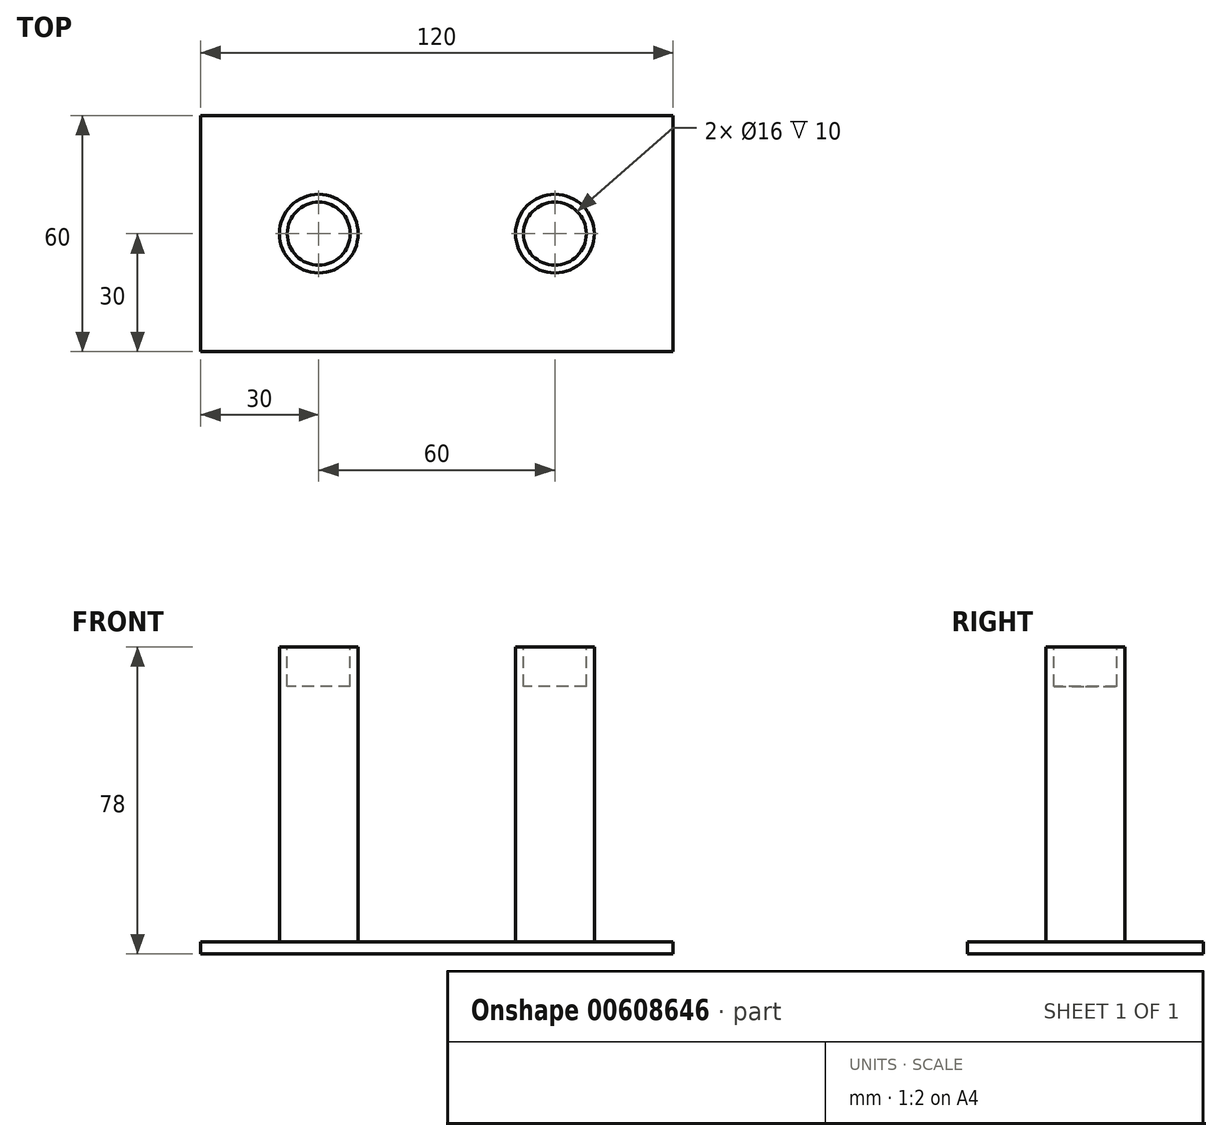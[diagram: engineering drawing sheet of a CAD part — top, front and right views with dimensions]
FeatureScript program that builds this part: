
annotation { "Feature Type Name" : "Feature", "Feature Type Description" : "" }
export const myFeature = defineFeature(function(context is Context, id is Id, definition is map)
    precondition{}
    {
        {
            var Q0;
            Q0=qCreatedBy(makeId("Top.planeOp"),FACE);
            var sketch = newSketch(context, id + "F0", { "sketchPlane" : qUnion([Q0])});
            skCircle(sketch, "E0", {"center": v(0, 0) * mm, "radius": 10 * mm});
            skLineSegment(sketch, "E1", {"start": v(0, 0) * mm, "end": v(-60, 0) * mm, "construction": true});
            skCircle(sketch, "E2", {"center": v(-60, 0) * mm, "radius": 10 * mm});
            skLineSegment(sketch, "E3.bottom", {"start": v(-90, 30) * mm, "end": v(30, 30) * mm});
            skLineSegment(sketch, "E3.top", {"start": v(-90, -30) * mm, "end": v(30, -30) * mm});
            skLineSegment(sketch, "E3.left", {"start": v(-90, 30) * mm, "end": v(-90, -30) * mm});
            skLineSegment(sketch, "E3.right", {"start": v(30, 30) * mm, "end": v(30, -30) * mm});
            skSolve(sketch);
        }
        {
            var Q0;
            Q0=makeQuery(id+"F0.imprint","IMPRINT",FACE,{"disambiguationData":[TD([[makeQuery(id+"F0.imprint","IMPRINT",EDGE,{"derivedFrom":sQuery(id+"F0.wireOp",EDGE,"E0")}),-1.0]])]});
            var Q1;
            Q1=makeQuery(id+"F0.imprint","IMPRINT",FACE,{"disambiguationData":[TD([[makeQuery(id+"F0.imprint","IMPRINT",EDGE,{"derivedFrom":sQuery(id+"F0.wireOp",EDGE,"E2")}),1.0]])]});
            var Q2;
            Q2=makeQuery(id+"F0.imprint","IMPRINT",FACE,{"disambiguationData":[TD([[makeQuery(id+"F0.imprint","IMPRINT",EDGE,{"derivedFrom":sQuery(id+"F0.wireOp",EDGE,"E0")}),1.0]])]});
            extrude(context, id + "F1", {"entities" : qUnion([Q0, Q1, Q2]), "oppositeDirection" : true, "depth" : 3 * mm, "offsetDistance" : 25 * mm});
        }
        {
            var Q0;
            Q0=makeQuery(id+"F0.imprint","IMPRINT",FACE,{"disambiguationData":[TD([[makeQuery(id+"F0.imprint","IMPRINT",EDGE,{"derivedFrom":sQuery(id+"F0.wireOp",EDGE,"E2")}),1.0]])]});
            var Q1;
            Q1=makeQuery(id+"F0.imprint","IMPRINT",FACE,{"disambiguationData":[TD([[makeQuery(id+"F0.imprint","IMPRINT",EDGE,{"derivedFrom":sQuery(id+"F0.wireOp",EDGE,"E0")}),1.0]])]});
            extrude(context, id + "F2", {"entities" : qUnion([Q0, Q1]), "operationType" : NewBodyOperationType.ADD, "depth" : 75 * mm, "offsetDistance" : 25 * mm});
        }
        {
            var Q0;
            Q0=makeQuery(id+"F2.opExtrude","CAP_FACE",FACE,{"disambiguationData":[OSD([sQuery(id+"F0.wireOp",EDGE,"E2")])],"isStart":false});
            var sketch = newSketch(context, id + "F3", { "sketchPlane" : qUnion([Q0])});
            skCircle(sketch, "E4", {"center": v(-60, 0) * mm, "radius": 8 * mm});
            skCircle(sketch, "E5", {"center": v(0, 0) * mm, "radius": 8 * mm});
            skSolve(sketch);
        }
        {
            var Q0;
            Q0=makeQuery(id+"F3.imprint","IMPRINT",FACE,{"disambiguationData":[TD([[makeQuery(id+"F3.imprint","IMPRINT",EDGE,{"derivedFrom":sQuery(id+"F3.wireOp",EDGE,"E4")}),1.0]])]});
            var Q1;
            Q1=makeQuery(id+"F3.imprint","IMPRINT",FACE,{"disambiguationData":[TD([[makeQuery(id+"F3.imprint","IMPRINT",EDGE,{"derivedFrom":sQuery(id+"F3.wireOp",EDGE,"E5")}),1.0]])]});
            extrude(context, id + "F4", {"entities" : qUnion([Q0, Q1]), "operationType" : NewBodyOperationType.REMOVE, "oppositeDirection" : true, "depth" : 10 * mm, "offsetDistance" : 25 * mm});
        }
    });
